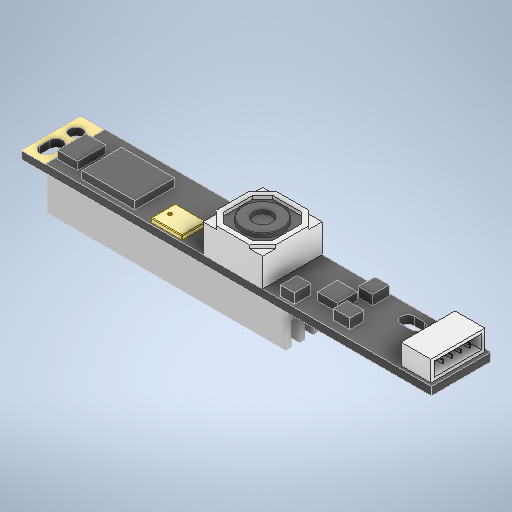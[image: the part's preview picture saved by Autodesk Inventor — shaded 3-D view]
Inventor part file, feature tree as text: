
AUTODESK INVENTOR PART (.ipt)
format: ipt  version: 2025 (Build 290162000, 162)  size: 456,704 bytes
history: native  units: mm
features: extrude x2, sketch x2, projected_geometry x2, plane x1, split x1
ambient origin geometry x8: Origin, YZ Plane, XZ Plane, XY Plane, X Axis, Y Axis, Z Axis, Center Point
bodies: Solid1 (feature_tree), Solid2 (feature_tree), Solid3 (feature_tree), Solid4 (feature_tree), Solid5 (feature_tree), Solid6 (feature_tree), Solid7 (feature_tree), Solid8 (feature_tree), Solid9 (feature_tree), Solid10 (feature_tree)
feature tree (8):
  extrude  "Extrusion1"  Depth=36.0mm
  plane  "Work Plane1"
  split  "Split1"
  extrude  "Extrusion2"  Depth=0.8mm
  sketch  "Sketch1"  dims[d0=4.0mm d1=36.0mm]
  projected_geometry  "Projected Loop1"
  sketch  "Sketch2"  dims[d2=5.0mm d3=0.0mm d5=0.8mm d6=1.5mm d7=0.0mm d8=0.0mm]
  projected_geometry  "Projected Loop2"
